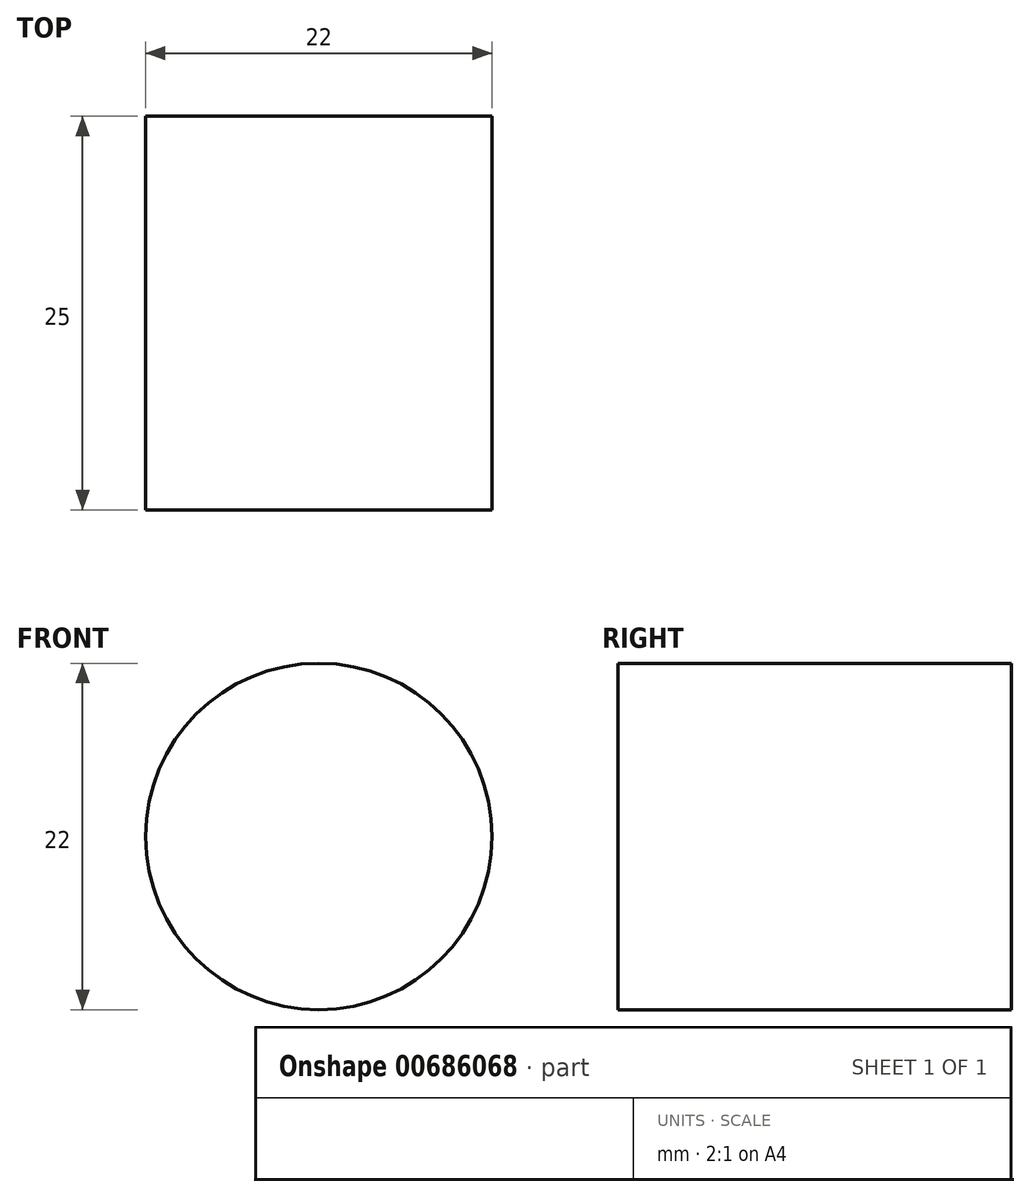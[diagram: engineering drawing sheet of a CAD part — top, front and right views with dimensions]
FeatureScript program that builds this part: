
annotation { "Feature Type Name" : "Feature", "Feature Type Description" : "" }
export const myFeature = defineFeature(function(context is Context, id is Id, definition is map)
    precondition{}
    {
        {
            var Q0;
            Q0=qCreatedBy(makeId("Front.planeOp"),FACE);
            var sketch = newSketch(context, id + "F0", { "sketchPlane" : qUnion([Q0])});
            skCircle(sketch, "E0", {"center": v(0, 0) * mm, "radius": 11 * mm});
            skSolve(sketch);
        }
        {
            var Q0;
            Q0=makeQuery(id+"F0.imprint","IMPRINT",FACE,{"disambiguationData":[TD([[makeQuery(id+"F0.imprint","IMPRINT",EDGE,{"derivedFrom":sQuery(id+"F0.wireOp",EDGE,"E0")}),1.0]])]});
            extrude(context, id + "F1", {"entities" : qUnion([Q0]), "depth" : 25 * mm, "offsetDistance" : 25 * mm});
        }
    });
